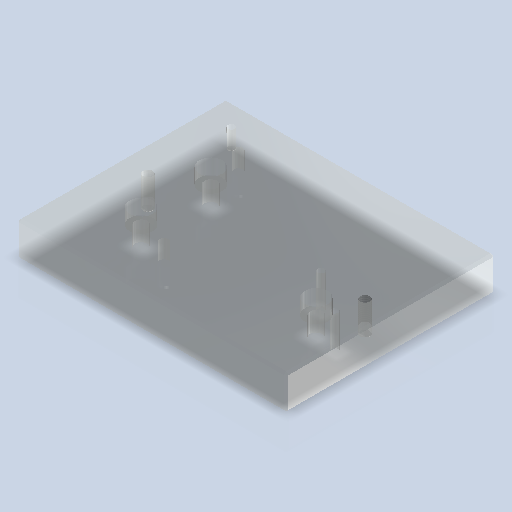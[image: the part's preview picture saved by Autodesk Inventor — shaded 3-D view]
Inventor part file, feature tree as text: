
AUTODESK INVENTOR PART (.ipt)
format: ipt  version: 2024.2 (Build 282272000, 272)  size: 324,608 bytes
history: native  units: mm
features: sketch x8, hole x7, extrude x1, chamfer x1
ambient origin geometry x8: Origin, YZ Plane, XZ Plane, XY Plane, X Axis, Y Axis, Z Axis, Center Point
bodies: Volumenkörper1 (feature_tree)
feature tree (17):
  extrude  "Extrusion1"  Depth=90.0mm
  hole  "Bohrung1"  [1 undecoded]
  hole  "Bohrung3"  [1 undecoded]
  hole  "Bohrung4"  [1 undecoded]
  hole  "Bohrung5"  [1 undecoded]
  hole  "Bohrung6"  [1 undecoded]
  hole  "Bohrung7"  [1 undecoded]
  hole  "Bohrung8"  [1 undecoded]
  chamfer  "Fasen1"  Distance=18.0mm
  sketch  "Skizze1"  dims[d0=116.0mm d1=90.0mm]
  sketch  "Skizze2"  dims[d2=15.0mm d3=0.0mm]
  sketch  "Skizze4"  dims[d4=4.134mm d5=10.0mm d6=4.0mm d7=2.0mm d8=90.0deg d9=13.0mm d10=20.594885mm d11=11.0mm]
  sketch  "Skizze5"  dims[d20=35.0mm d21=61.0mm]
  sketch  "Skizze6"  dims[d22=22.0mm d23=71.5mm]
  sketch  "Skizze7"  dims[d24=5.5mm d25=6.0mm d26=10.0mm d27=6.5mm d28=90.0deg d29=8.0mm d30=20.594885mm]
  sketch  "Skizze8"  dims[d31=4.134mm d32=10.0mm d33=10.0mm d34=6.5mm d35=90.0deg d36=13.0mm d37=20.594885mm d38=93.572079mm]
  sketch  "Skizze10"  dims[d39=30.0mm d40=5.5mm d41=10.0mm d42=10.0mm d43=6.5mm d44=90.0deg d45=5.5mm d46=0.0mm d47=3.0mm d48=6.0mm d49=10.0mm d50=6.5mm d51=90.0deg d52=8.0mm d53=20.594885mm d54=4.0mm d55=6.0mm d56=4.0mm d57=2.0mm d58=90.0deg d59=8.0mm d60=20.594885mm d61=50.0mm d62=30.0mm d63=18.0mm d64=3.0mm d65=6.0mm d66=4.0mm d67=2.0mm d68=90.0deg d69=8.0mm d70=20.594885mm d71=18.0mm d72=31.0mm d73=34.0mm d74=12.0mm d75=1.0mm d76=2.0mm d77=45.0deg]
note: 7 required parameter values undecoded (feature->parameter linkage not recoverable at this tier; creation-order binding heuristic only, values carry confidence <= 0.55)
